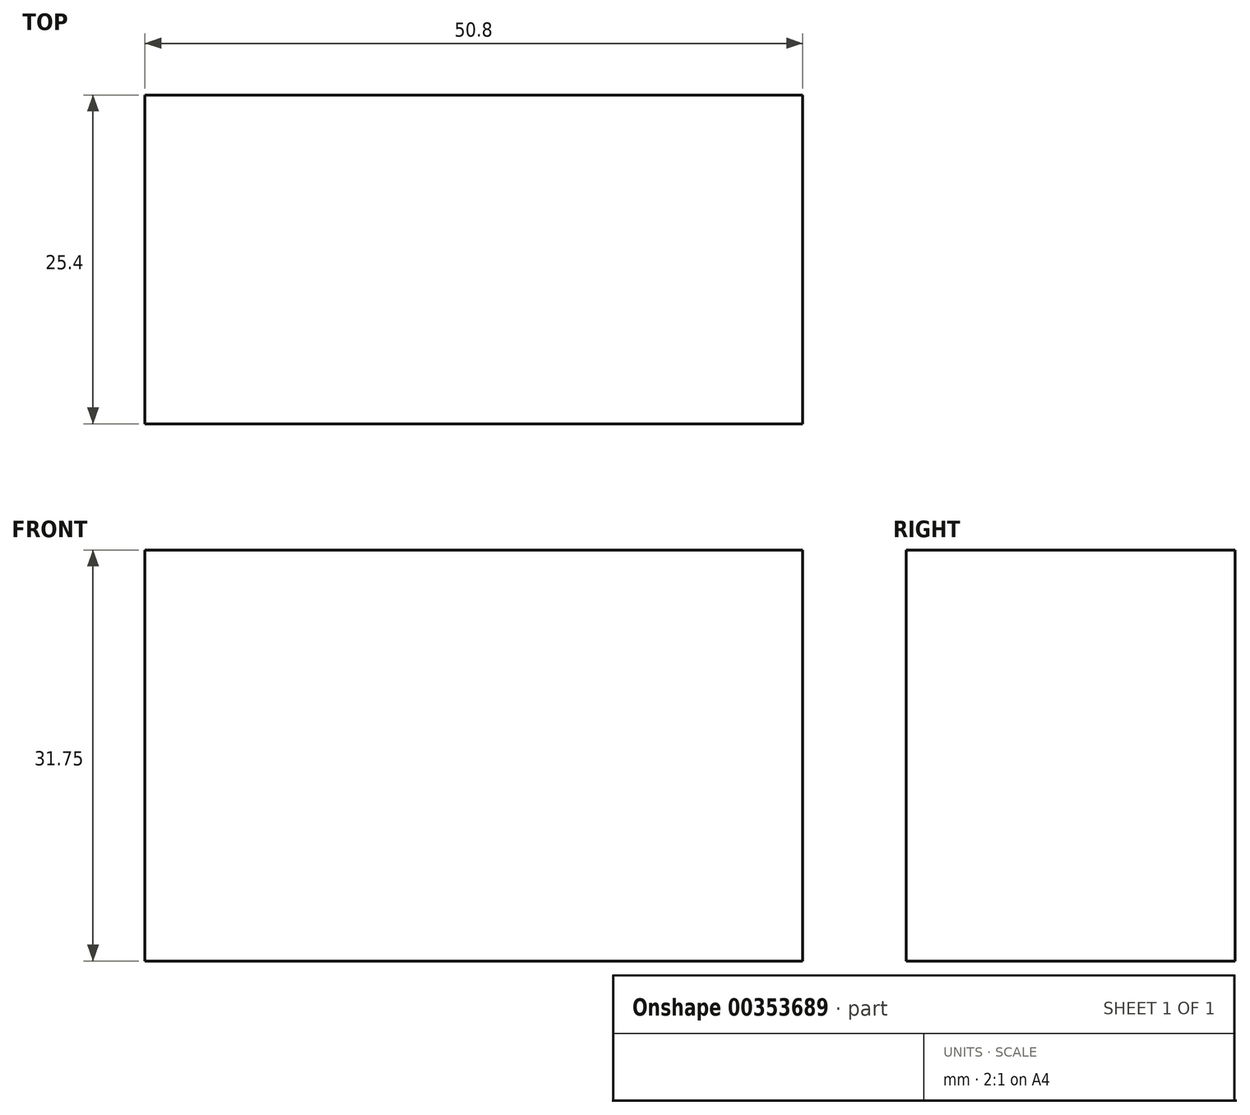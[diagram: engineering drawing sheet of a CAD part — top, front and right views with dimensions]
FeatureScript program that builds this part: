
annotation { "Feature Type Name" : "Feature", "Feature Type Description" : "" }
export const myFeature = defineFeature(function(context is Context, id is Id, definition is map)
    precondition{}
    {
        {
            var Q0;
            Q0=qCreatedBy(makeId("Front.planeOp"),FACE);
            var sketch = newSketch(context, id + "F0", { "sketchPlane" : qUnion([Q0])});
            skLineSegment(sketch, "E0", {"start": v(-32.06, 9.64) * mm, "end": v(-32.06, -22.11) * mm});
            skLineSegment(sketch, "E1", {"start": v(-32.06, -22.11) * mm, "end": v(18.74, -22.11) * mm});
            skLineSegment(sketch, "E2", {"start": v(18.74, -22.11) * mm, "end": v(18.74, 9.64) * mm});
            skLineSegment(sketch, "E3", {"start": v(18.74, 9.64) * mm, "end": v(-32.06, 9.64) * mm});
            skSolve(sketch);
        }
        {
            var Q0;
            Q0=makeQuery(id+"F0.imprint","IMPRINT",FACE,{"disambiguationData":[TD([[makeQuery(id+"F0.imprint","IMPRINT",EDGE,{"derivedFrom":sQuery(id+"F0.wireOp",EDGE,"E0")}),1.0]])]});
            extrude(context, id + "F1", {"entities" : qUnion([Q0]), "depth" : 25.4 * mm});
        }
        {
            var Q0;
            Q0=makeQuery(id+"F1.opExtrude","SWEPT_FACE",FACE,{"disambiguationData":[OSD([sQuery(id+"F0.wireOp",EDGE,"E2")])]});
            var sketch = newSketch(context, id + "F2", { "sketchPlane" : qUnion([Q0])});
            skLineSegment(sketch, "E4", {"start": v(-12.7, 9.64) * mm, "end": v(-12.7, -11.63) * mm});
            skLineSegment(sketch, "E5", {"start": v(-12.7, -11.63) * mm, "end": v(-25.4, -11.63) * mm});
            skLineSegment(sketch, "E6", {"start": v(-25.4, -11.63) * mm, "end": v(-25.4, 9.64) * mm});
            skLineSegment(sketch, "E7", {"start": v(-25.4, 9.64) * mm, "end": v(-12.7, 9.64) * mm});
            skSolve(sketch);
        }
        {
            var Q0;
            Q0=makeQuery(id+"F2.imprint","IMPRINT",FACE,{"disambiguationData":[TD([[makeQuery(id+"F2.imprint","IMPRINT",EDGE,{"derivedFrom":sQuery(id+"F2.wireOp",EDGE,"E4")}),-1.0]])]});
            extrude(context, id + "F3", {"entities" : qUnion([Q0]), "operationType" : NewBodyOperationType.ADD, "depth" : 50.8 * mm});
        }
        {
            var Q0;
            Q0=makeQuery(id+"F3.opExtrude","CAP_FACE",FACE,{"disambiguationData":[OSD([sQuery(id+"F2.wireOp",EDGE,"E4"),sQuery(id+"F2.wireOp",EDGE,"E5"),sQuery(id+"F2.wireOp",EDGE,"E6"),sQuery(id+"F2.wireOp",EDGE,"E7")])],"isStart":false});
            extrude(context, id + "F4", {"entities" : qUnion([Q0]), "operationType" : NewBodyOperationType.REMOVE, "oppositeDirection" : true, "depth" : 50.8 * mm});
        }
    });
